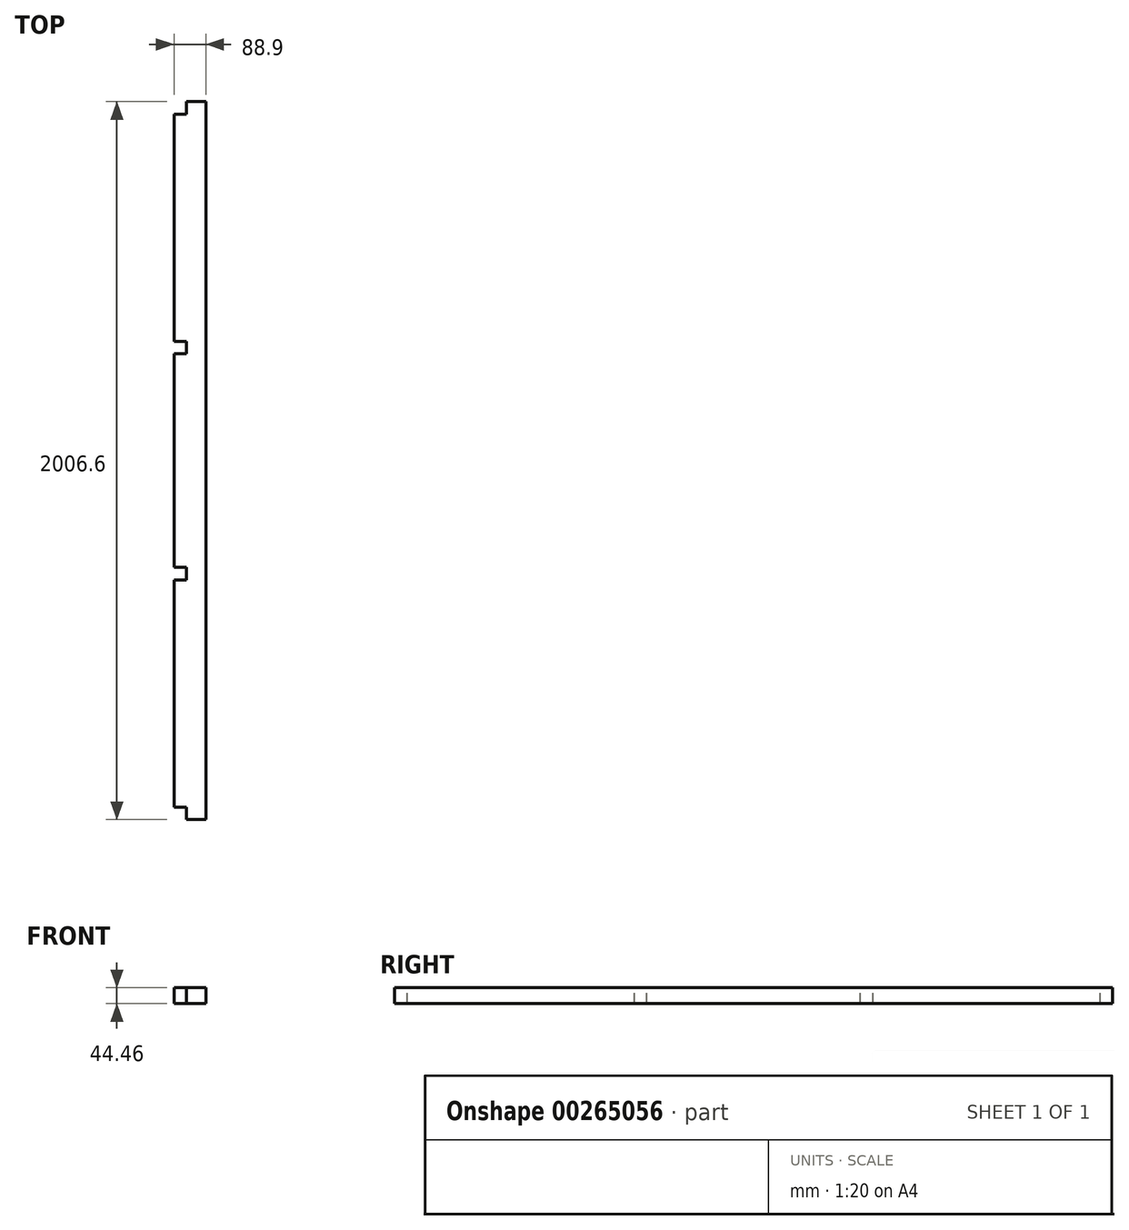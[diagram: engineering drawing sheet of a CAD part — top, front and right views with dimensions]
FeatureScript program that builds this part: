
annotation { "Feature Type Name" : "Feature", "Feature Type Description" : "" }
export const myFeature = defineFeature(function(context is Context, id is Id, definition is map)
    precondition{}
    {
        {
            var Q0;
            Q0=qCreatedBy(makeId("Front.planeOp"),FACE);
            var sketch = newSketch(context, id + "F0", { "sketchPlane" : qUnion([Q0])});
            skLineSegment(sketch, "E0.bottom", {"start": v(44.45, 22.23) * mm, "end": v(-44.45, 22.23) * mm});
            skLineSegment(sketch, "E0.top", {"start": v(44.45, -22.23) * mm, "end": v(-44.45, -22.23) * mm});
            skLineSegment(sketch, "E0.left", {"start": v(44.45, 22.23) * mm, "end": v(44.45, -22.23) * mm});
            skLineSegment(sketch, "E0.right", {"start": v(-44.45, 22.23) * mm, "end": v(-44.45, -22.23) * mm});
            skPoint(sketch, "E0.middle", {"position": v(0, 0) * mm});
            skSolve(sketch);
        }
        {
            var Q0;
            Q0 = qSketchRegion(id + "F0", true);
            extrude(context, id + "F1", {"entities" : qUnion([Q0]), "depth" : 2006.6 * mm});
        }
        {
            var Q0;
            Q0=makeQuery(id+"F1.opExtrude","SWEPT_FACE",FACE,{"disambiguationData":[OSD([sQuery(id+"F0.wireOp",EDGE,"E0.bottom")])]});
            var sketch = newSketch(context, id + "F2", { "sketchPlane" : qUnion([Q0])});
            skLineSegment(sketch, "E1.bottom", {"start": v(-44.45, 0) * mm, "end": v(-9.53, 0) * mm});
            skLineSegment(sketch, "E1.top", {"start": v(-44.45, -34.92) * mm, "end": v(-9.53, -34.92) * mm});
            skLineSegment(sketch, "E1.left", {"start": v(-44.45, 0) * mm, "end": v(-44.45, -34.92) * mm});
            skLineSegment(sketch, "E1.right", {"start": v(-9.53, 0) * mm, "end": v(-9.53, -34.92) * mm});
            skLineSegment(sketch, "E2.bottom", {"start": v(-44.45, -704.85) * mm, "end": v(-9.52, -704.85) * mm});
            skLineSegment(sketch, "E2.top", {"start": v(-44.45, -669.92) * mm, "end": v(-9.52, -669.92) * mm});
            skLineSegment(sketch, "E2.left", {"start": v(-44.45, -704.85) * mm, "end": v(-44.45, -669.92) * mm});
            skLineSegment(sketch, "E2.right", {"start": v(-9.53, -704.85) * mm, "end": v(-9.53, -669.92) * mm});
            skLineSegment(sketch, "E3.bottom", {"start": v(-44.45, -2006.6) * mm, "end": v(-9.53, -2006.6) * mm});
            skLineSegment(sketch, "E3.top", {"start": v(-44.45, -1971.67) * mm, "end": v(-9.53, -1971.67) * mm});
            skLineSegment(sketch, "E3.left", {"start": v(-44.45, -2006.6) * mm, "end": v(-44.45, -1971.67) * mm});
            skLineSegment(sketch, "E3.right", {"start": v(-9.53, -2006.6) * mm, "end": v(-9.53, -1971.67) * mm});
            skLineSegment(sketch, "E4.bottom", {"start": v(-44.45, -1301.75) * mm, "end": v(-9.53, -1301.75) * mm});
            skLineSegment(sketch, "E4.top", {"start": v(-44.45, -1336.67) * mm, "end": v(-9.53, -1336.67) * mm});
            skLineSegment(sketch, "E4.left", {"start": v(-44.45, -1301.75) * mm, "end": v(-44.45, -1336.67) * mm});
            skLineSegment(sketch, "E4.right", {"start": v(-9.53, -1301.75) * mm, "end": v(-9.53, -1336.67) * mm});
            skSolve(sketch);
        }
        {
            var Q0;
            Q0=makeQuery(id+"F2.imprint","IMPRINT",FACE,{"disambiguationData":[TD([[makeQuery(id+"F2.imprint","IMPRINT",EDGE,{"derivedFrom":sQuery(id+"F2.wireOp",EDGE,"E1.bottom")}),1.0]])]});
            var Q1;
            Q1=makeQuery(id+"F2.imprint","IMPRINT",FACE,{"disambiguationData":[TD([[makeQuery(id+"F2.imprint","IMPRINT",EDGE,{"derivedFrom":sQuery(id+"F2.wireOp",EDGE,"E3.bottom")}),-1.0]])]});
            var Q2;
            Q2=makeQuery(id+"F2.imprint","IMPRINT",FACE,{"disambiguationData":[TD([[makeQuery(id+"F2.imprint","IMPRINT",EDGE,{"derivedFrom":sQuery(id+"F2.wireOp",EDGE,"E4.bottom")}),-1.0]])]});
            var Q3;
            Q3=makeQuery(id+"F2.imprint","IMPRINT",FACE,{"disambiguationData":[TD([[makeQuery(id+"F2.imprint","IMPRINT",EDGE,{"derivedFrom":sQuery(id+"F2.wireOp",EDGE,"E2.bottom")}),1.0]])]});
            extrude(context, id + "F3", {"entities" : qUnion([Q0, Q1, Q2, Q3]), "operationType" : NewBodyOperationType.REMOVE, "oppositeDirection" : true, "depth" : 50.8 * mm});
        }
    });
